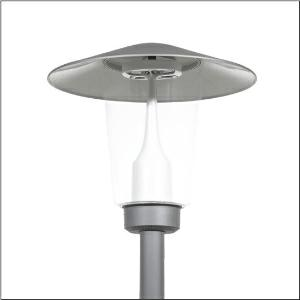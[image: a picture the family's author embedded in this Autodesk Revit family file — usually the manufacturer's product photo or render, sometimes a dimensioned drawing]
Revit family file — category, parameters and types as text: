
# Revit family: pilzleuchte_iq___st1_2a_5xa5235mf14hp_ceaa
name_source: partatom
category: Lighting Fixtures
units: mm (PartAtom-declared; Revit-internal decimal feet)

## family parameters
Cut with Voids When Loaded = No
Host = Face
Light Source = No
Part Type = Normal
Room Calculation Point = No
Round Connector Dimension = Use Diameter
Shared = No

## types (1)
- --- (1 x LED, 4280 lm, 33.6 W, 2700K)
    Apparent Load = 34 VA
    CIE Flux Codes = 23 60 92 98 100
    Color Rendering = 70
    Color Temperature = 2700K
    Default Elevation = 1800 mm
    Description = Mushroom Luminaire iQ, mast luminaire, Module 540 iQ-SR, primary light control with 3 zone facetted reflector, of plastic, silver coated, highly specular, structured, primary optical cover: cover, of PMMA, transparent, light distribution: ST1.2a, light emission: direct distribution, primary light characteristic: asymmetric, installation type: post-top, LED, High Power LED, rated luminous flux: 4.280lm, luminous efficacy: 127lm/W, light colour: 727, colour temperature: 2700K, control gear: ECG iQ, control: pre-setting: logarithmic dimming characteristic, Street-Remote, Auto-Match, Temp-Guard, Lumen-Switch, Night-Set, Smart-Wire, Light-Fading, Desk-Remote (wireless, voltage-free reading and setting of iQ features in the workshop via application-optimized NFC function/RFID function), optimised constant luminous flux control (CLO 2.0), with terminal, 6-pole, max. 2.5mm², mains connection: 230..240V, AC, 50/60Hz, start of lifetime: 34W, end of service life: 36W, reduction: 15W, luminaire housing, upper part, of glass-fibre reinforced polyester, coated, Siteco® metallic grey (DB 702S), diameter: 650mm, height: 586mm, spigot size: d x l = 76 x 70mm (post-top) | with reducer (optional accessory) 60 x 70mm, post-top mast mounting element, of diecast aluminium, coated, Siteco® metallic grey (DB 702S), Module 540 iQ-SR, traffic white (RAL 9016), equipment: Power, protection rating (complete): IP65, insulation class (complete): insulation class II (safety insulation), certification: CE, ENEC, VDE, packaging unit: 1 piece

Light Distribution: ST1.2a
    Height = 586 mm
    Lamp = 1 x LED
    Lamp Light Flux = 4280 lm
    Lamp Power = 33.6 W
    Lamp count = 1
    Length = 650 mm
    Luminous efficacy = 127 lm/W
    Manufacturer = Siteco
    ModVariant = No
    Model = 5XA5235MF14HP
    Number of Poles = 1
    OnlyDefault = Yes
    Power Factor = 1
    Product Name = Pilzleuchte iQ | ST1.2a
    Product group = mast luminaire | pylon top
    ProductGroupID = 6100
    Protection Class = Protection class II
    Protection Degree = IP 65
    RLX_Detail_Level = 1
    RLX_Emergency_Light_Flux = 0 lm
    RLX_Emergency_Type = 0
    RLX_Emergency_Type_DB = No
    RlxData = <blob elided: 51629 chars, md5=a0f11d39>
    Socket = socket
    Standby Power = 0 W
    System Light Flux = 4280 lm
    System Power = 34 W
    Type Comments = factory setting: luminous flux: 100 % | dim-lin: 254 | 695 mA
    Type Image = l_1006077.jpg
    URL = http://relux.com
    VarID = @adj_123141
    Voltage = 0 V
    Weight = 0.00 kg
    Width = 0 mm  [stored 0 ft]

note: [stored X ft] marks values corroborated as IEEE doubles in the binary element streams (Revit-internal decimal feet)

## geometry (parser evidence)
native form markers: Blend x4, Sweep x11
no freeform markers — native parametric forms only
